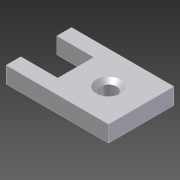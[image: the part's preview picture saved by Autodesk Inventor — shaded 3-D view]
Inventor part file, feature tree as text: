
AUTODESK INVENTOR PART (.ipt)
format: ipt  version: 2013 (Build 170138000, 138)  size: 82,944 bytes
history: native  units: mm
features: sketch x2, reference x2, extrude x1, hole x1
ambient origin geometry x8: Origin, YZ Plane, XZ Plane, XY Plane, X Axis, Y Axis, Z Axis, Center Point
bodies: Volumenkörper1 (feature_tree)
feature tree (6):
  extrude  "Extrusion1"  Depth=2.0mm
  hole  "Bohrung1"  [1 undecoded]
  sketch  "Skizze1"  dims[d0=4.0mm d1=2.0mm]
  reference  "Referenz1"
  reference  "Referenz2"
  sketch  "Skizze3"  dims[d2=2.0mm d5=1.0mm d6=0.0mm d7=2.0mm d8=2.0mm d11=1.0mm d12=6.0mm d13=1.5mm d14=2.0mm d15=90.0deg d16=8.0mm d17=20.594885mm d18=6.261895mm]
note: 1 required parameter value undecoded (feature->parameter linkage not recoverable at this tier; creation-order binding heuristic only, values carry confidence <= 0.55)
